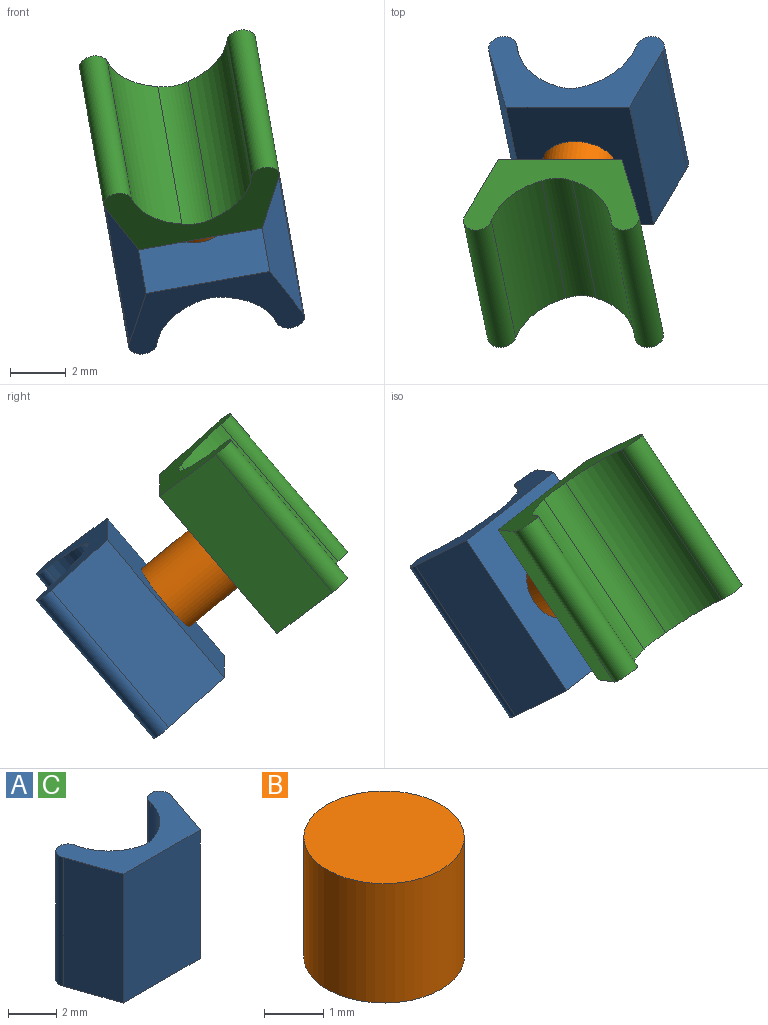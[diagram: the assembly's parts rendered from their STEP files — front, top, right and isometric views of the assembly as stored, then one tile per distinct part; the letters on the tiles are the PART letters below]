
ASSEMBLY  parts=3 mates=2
PART A: 10 faces, bbox 6.4x3.3x6.5 mm
  f0: cylinder r=0.51mm len=6.53mm, axis (0,0,-1), area 11.3mm2, adj f1,f7,f8,f9
  f1: plane 6.53x2.6mm, normal (-0.94,-0.33,0), area 18mm2, adj f0,f2,f8,f9
  f2: plane 6.53x4.5mm, normal (0,-1,0), area 29.4mm2, adj f1,f3,f8,f9
  f3: plane 6.53x2.6mm, normal (0.94,-0.33,0), area 18mm2, adj f2,f4,f8,f9
  f4: cylinder r=0.51mm len=6.53mm, axis (0,0,-1), area 11.3mm2, adj f3,f5,f8,f9
  f5: cylinder r=2.56mm len=6.53mm, axis (0,0,-1), area 16.8mm2, adj f4,f6,f8,f9
  f6: cylinder r=1.27mm len=6.53mm, axis (0,0,-1), area 7.5mm2, adj f5,f7,f8,f9
  f7: cylinder r=2.56mm len=6.53mm, axis (0,0,-1), area 16.8mm2, adj f0,f6,f8,f9
  f8: plane 6.39x3.3mm, normal (0,0,1), area 10.2mm2, adj f0,f1,f2,f3,f4,f5,f6,f7
  f9: plane 6.39x3.3mm, normal (0,0,-1), area 10.2mm2, adj f0,f1,f2,f3,f4,f5,f6,f7
PART B: 3 faces, bbox 2.7x2.7x2.5 mm
  f0: cylinder r=1.35mm len=2.7mm, axis (0,0,-1), area 20.9mm2, adj f1,f2
  f1: plane 2.7x2.7mm, normal (0,0,1), area 5.7mm2, adj f0
  f2: plane 2.7x2.7mm, normal (0,0,-1), area 5.7mm2, adj f0
PART C: same geometry as A
PLACE A rot(axis=(-0.97,-0.23,-0.08),41.2deg) t=(8.64,-0.88,0.92)mm
PLACE B rot(axis=(0.98,-0.18,0.09),50.9deg) t=(8.21,1.22,3.38)mm
PLACE C rot(axis=(1,-0.03,0.09),140.2deg) t=(7.5,1.43,7.4)mm
MATE fastened B.f0 <-> A.f2  axis (0.11,0.77,-0.63) through (8.21,1.22,3.38)mm
MATE fastened C.f2 <-> B.f0  axis (0.11,0.77,-0.63) through (7.93,-0.66,4.94)mm
